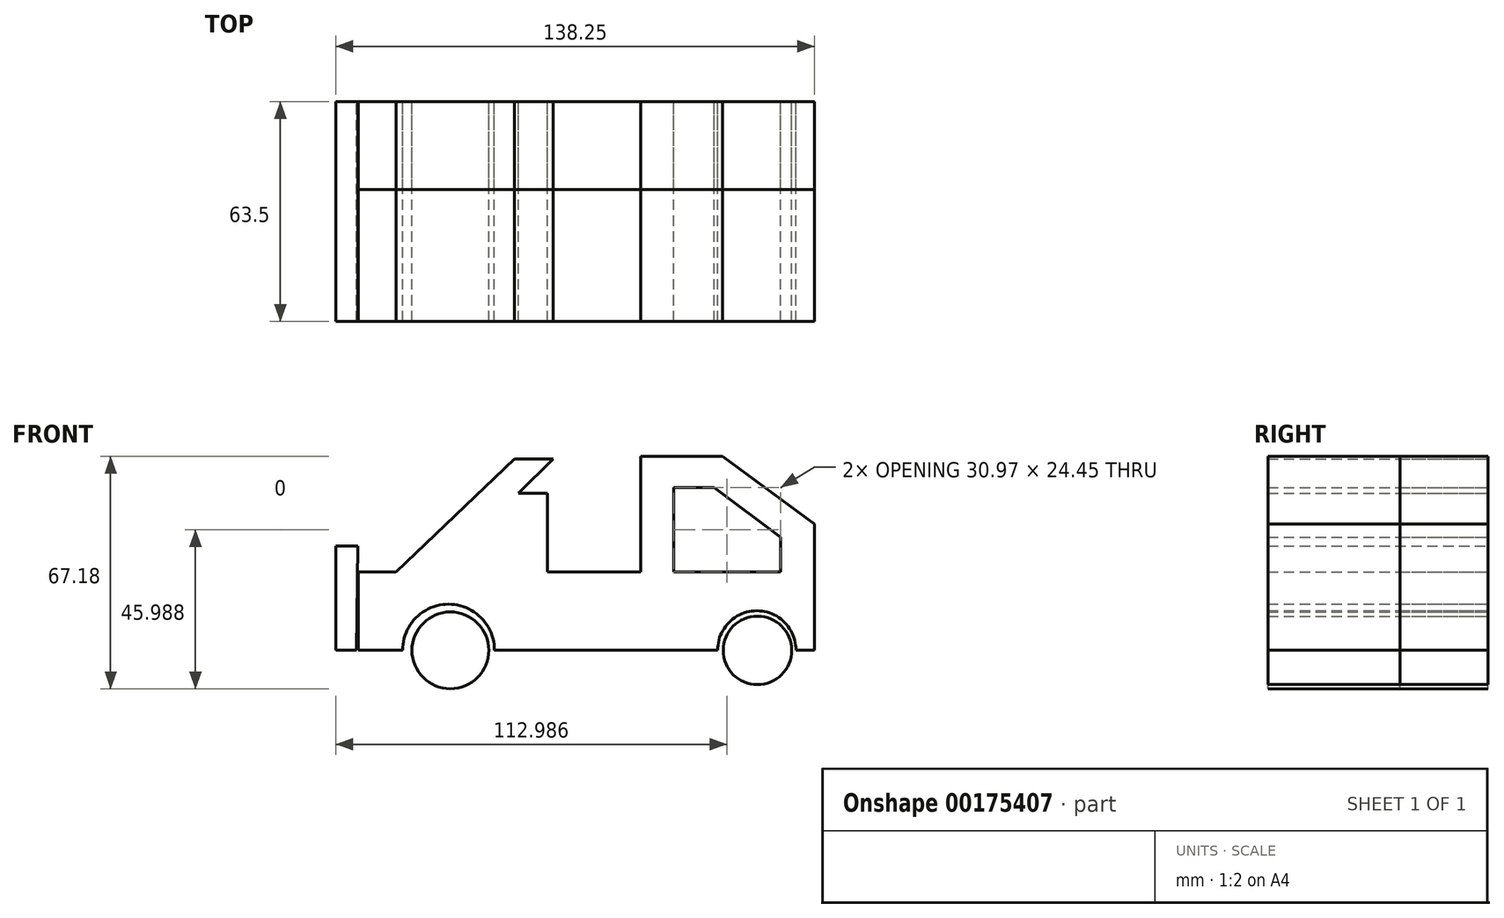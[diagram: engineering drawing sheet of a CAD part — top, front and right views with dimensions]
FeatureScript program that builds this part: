
annotation { "Feature Type Name" : "Feature", "Feature Type Description" : "" }
export const myFeature = defineFeature(function(context is Context, id is Id, definition is map)
    precondition{}
    {
        {
            var Q0;
            Q0=qCreatedBy(makeId("Front.planeOp"),FACE);
            var sketch = newSketch(context, id + "F0", { "sketchPlane" : qUnion([Q0])});
            skCircle(sketch, "E0", {"center": v(-39.72, 0) * mm, "radius": 11.1 * mm});
            skCircle(sketch, "E1", {"center": v(48.93, 0) * mm, "radius": 9.9 * mm});
            skArc(sketch, "E2", {"start": v(-27, 0) * mm, "mid": v(-40.25, 13.34) * mm, "end": v(-53.5, 0) * mm});
            skArc(sketch, "E3", {"start": v(60.06, 0) * mm, "mid": v(48.75, 11.44) * mm, "end": v(37.44, 0) * mm});
            skLineSegment(sketch, "E4", {"start": v(-27, 0) * mm, "end": v(37.44, 0) * mm});
            skLineSegment(sketch, "E5", {"start": v(-53.5, 0) * mm, "end": v(-66.31, 0) * mm});
            skLineSegment(sketch, "E6", {"start": v(-66.31, 0) * mm, "end": v(-66.31, 22.65) * mm});
            skLineSegment(sketch, "E7", {"start": v(-66.31, 22.65) * mm, "end": v(15.18, 22.65) * mm});
            skLineSegment(sketch, "E8", {"start": v(15.18, 22.65) * mm, "end": v(15.18, 56.07) * mm});
            skLineSegment(sketch, "E9", {"start": v(15.18, 56.07) * mm, "end": v(38.82, 56.07) * mm});
            skLineSegment(sketch, "E10", {"start": v(38.82, 56.07) * mm, "end": v(65.44, 36.5) * mm});
            skLineSegment(sketch, "E11", {"start": v(65.44, 36.5) * mm, "end": v(65.44, 0) * mm});
            skLineSegment(sketch, "E12", {"start": v(65.44, 0) * mm, "end": v(60.06, 0) * mm});
            skLineSegment(sketch, "E13", {"start": v(24.7, 22.65) * mm, "end": v(24.7, 47.1) * mm});
            skLineSegment(sketch, "E14", {"start": v(24.7, 47.1) * mm, "end": v(36.37, 47.1) * mm});
            skLineSegment(sketch, "E15", {"start": v(36.37, 47.1) * mm, "end": v(55.66, 32.7) * mm});
            skLineSegment(sketch, "E16", {"start": v(55.66, 32.7) * mm, "end": v(55.66, 22.65) * mm});
            skLineSegment(sketch, "E17", {"start": v(55.66, 22.65) * mm, "end": v(24.7, 22.65) * mm});
            skLineSegment(sketch, "E18", {"start": v(-55.45, 22.65) * mm, "end": v(-21.22, 55.25) * mm});
            skLineSegment(sketch, "E19", {"start": v(-21.22, 55.25) * mm, "end": v(-10.08, 55.25) * mm});
            skLineSegment(sketch, "E20", {"start": v(-10.08, 55.25) * mm, "end": v(-42.95, 22.65) * mm});
            skLineSegment(sketch, "E21", {"start": v(-20.03, 45.38) * mm, "end": v(-20.03, 22.65) * mm});
            skLineSegment(sketch, "E22", {"start": v(-20.03, 45.38) * mm, "end": v(-11.7, 45.38) * mm});
            skLineSegment(sketch, "E23", {"start": v(-11.7, 45.38) * mm, "end": v(-11.7, 22.65) * mm});
            skSolve(sketch);
        }
        {
            var Q0;
            Q0 = qSketchRegion(id + "F0", true);
            extrude(context, id + "F1", {"entities" : qUnion([Q0]), "depth" : 25.4 * mm});
        }
        {
            var Q0;
            Q0 = qSketchRegion(id + "F0", true);
            extrude(context, id + "F2", {"entities" : qUnion([Q0]), "depth" : 63.5 * mm});
        }
        {
            var Q0;
            Q0=qCreatedBy(makeId("Front.planeOp"),FACE);
            var sketch = newSketch(context, id + "F3", { "sketchPlane" : qUnion([Q0])});
            skLineSegment(sketch, "E24", {"start": v(-66.77, 0) * mm, "end": v(-72.81, 0) * mm});
            skLineSegment(sketch, "E25", {"start": v(-72.81, 0) * mm, "end": v(-72.81, 30.22) * mm});
            skLineSegment(sketch, "E26", {"start": v(-72.81, 30.22) * mm, "end": v(-66.48, 30.22) * mm});
            skLineSegment(sketch, "E27", {"start": v(-66.48, 30.22) * mm, "end": v(-66.77, 0) * mm});
            skSolve(sketch);
        }
        {
            var Q0;
            Q0=makeQuery(id+"F3.imprint","IMPRINT",FACE,{"disambiguationData":[TD([[makeQuery(id+"F3.imprint","IMPRINT",EDGE,{"derivedFrom":sQuery(id+"F3.wireOp",EDGE,"E24")}),-1.0]])]});
            extrude(context, id + "F4", {"entities" : qUnion([Q0]), "depth" : 63.5 * mm});
        }
    });
